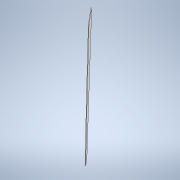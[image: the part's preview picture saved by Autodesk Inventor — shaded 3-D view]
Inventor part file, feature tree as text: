
AUTODESK INVENTOR PART (.ipt)
format: ipt  version: 2020.3 (Build 243373010, 373A)  size: 186,368 bytes
history: native  units: mm
features: other x38, extrude x1, sketch x1
ambient origin geometry x8: Origin, YZ Plane, XZ Plane, XY Plane, X Axis, Y Axis, Z Axis, Center Point
bodies: Solid1 (feature_tree)
feature tree (40):
  other  "base_sketch.ipt"
  other  "inner_surface"
  other  "outer_surface"
  other  "Work Point23"
  other  "Work Point28"
  other  "Work Point29"
  other  "Work Point30"
  other  "Work Point31"
  other  "Work Point32"
  extrude  "Extrusion1"  Depth=1.2mm
  other  "bulkhead_main"
  other  "bulkhead_F1"
  other  "bulkhead_front"
  other  "bulkhead_F2"
  other  "bulkhead_B1"
  other  "bulkhead_B2"
  other  "transom"
  other  "stinger_bottom_liner"
  other  "bulkhead_front_tunnel_top"
  other  "bulkhead_front_tunnel_bottom"
  other  "bulkhead_main_top"
  other  "bulkhead_main_tunnel_bottom"
  other  "bulkhead_main_tunnel_standoff"
  other  "bulkhead_front_top"
  other  "bulkhead_front_bottom"
  other  "bulkhead_F1_tunnel_bottom"
  other  "bulkhead_F1_tunnel_top"
  other  "bulkhead_F1_top"
  other  "bulkhead_F1_tunnel_standoff"
  other  "bulkhead_F1_bottom"
  other  "bulkhead_F2_bottom"
  other  "bulkhead_F2_top"
  other  "bulkhead_B1_bottom"
  other  "bulkhead_B1_top"
  other  "bulkhead_B1_tunnel_standoff"
  other  "bulkhead_B1_tunnel_bottom"
  other  "bulkhead_B2_top"
  other  "bulkhead_B2_tunnel_bottom"
  other  "bulkhead_B2_bottom"
  sketch  "Sketch11"  dims[d0=10.0mm d2=35.7mm d3=20.4mm d7=204.0mm d24=45.9mm d27=11.475mm d41=45.9mm d44=0.698132mm d45=122.4mm d48=27.54mm d50=49.7352mm d51=43.146mm d53=62.322mm d54=119.85mm d56=34.5168mm d57=11.5056mm d58=2.48676mm d61=33.558mm d63=0.918mm d66=62.322mm d67=19.176mm d68=19.176mm d70=9.18mm d71=15.0552mm d84=153.0mm d85=41.6925mm d86=102.0mm d87=42.84mm d90=40.8mm d91=24.48mm d95=10.2mm d97=10.340551mm d98=15.510827mm d100=8.541983mm d101=2.55mm d103=112.2mm d104=6.40305mm d105=6.885mm d106=17.2125mm d108=12.202833mm d110=3.582087mm d111=-102.0mm d112=-204.0mm d114=6.981317mm d115=6.981317mm d116=6.981317mm d119=11.760494mm d121=3.635062mm d123=0.729849mm d124=0.364924mm d126=2.390472mm d127=1.195236mm d131=48.8988mm d137=1.86507mm d30=306.0mm d49=45.9mm d55=57.528mm d64=19.176mm d65=18.36mm d96=34.468504mm d99=12.202833mm d107=12.202833mm d109=3.582087mm d120=21.382716mm d122=1.094773mm d125=3.585707mm d128=6.375647mm d130=57.528mm d136=2.48676mm d1=1.2mm d4=1.2mm d5=0.0mm]
